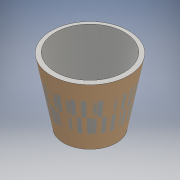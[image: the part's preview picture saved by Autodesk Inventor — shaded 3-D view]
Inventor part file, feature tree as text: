
AUTODESK INVENTOR PART (.ipt)
format: ipt  version: 2016 (Build 200138000, 138)  size: 118,784 bytes
history: native  units: mm
features: sketch x2, plane x1, thicken_offset x1, other x1, loft x1
ambient origin geometry x8: Origin, YZ Plane, XZ Plane, XY Plane, X Axis, Y Axis, Z Axis, Center Point
bodies: Body1 (feature_tree), Body2 (feature_tree)
feature tree (6):
  sketch  "Sketch1"  dims[d0=168.0mm d1=9.52mm]
  plane  "Work Plane1"
  thicken_offset  "Thicken1"
  sketch  "Sketch2"  dims[d2=-140.0mm d3=114.0mm d4=9.52mm d15=0.0mm d16=90.0deg d17=0.0mm d18=90.0deg d19=9.52mm d20=9.52mm]
  other  "Srf1"
  loft  "LoftSrf1"
